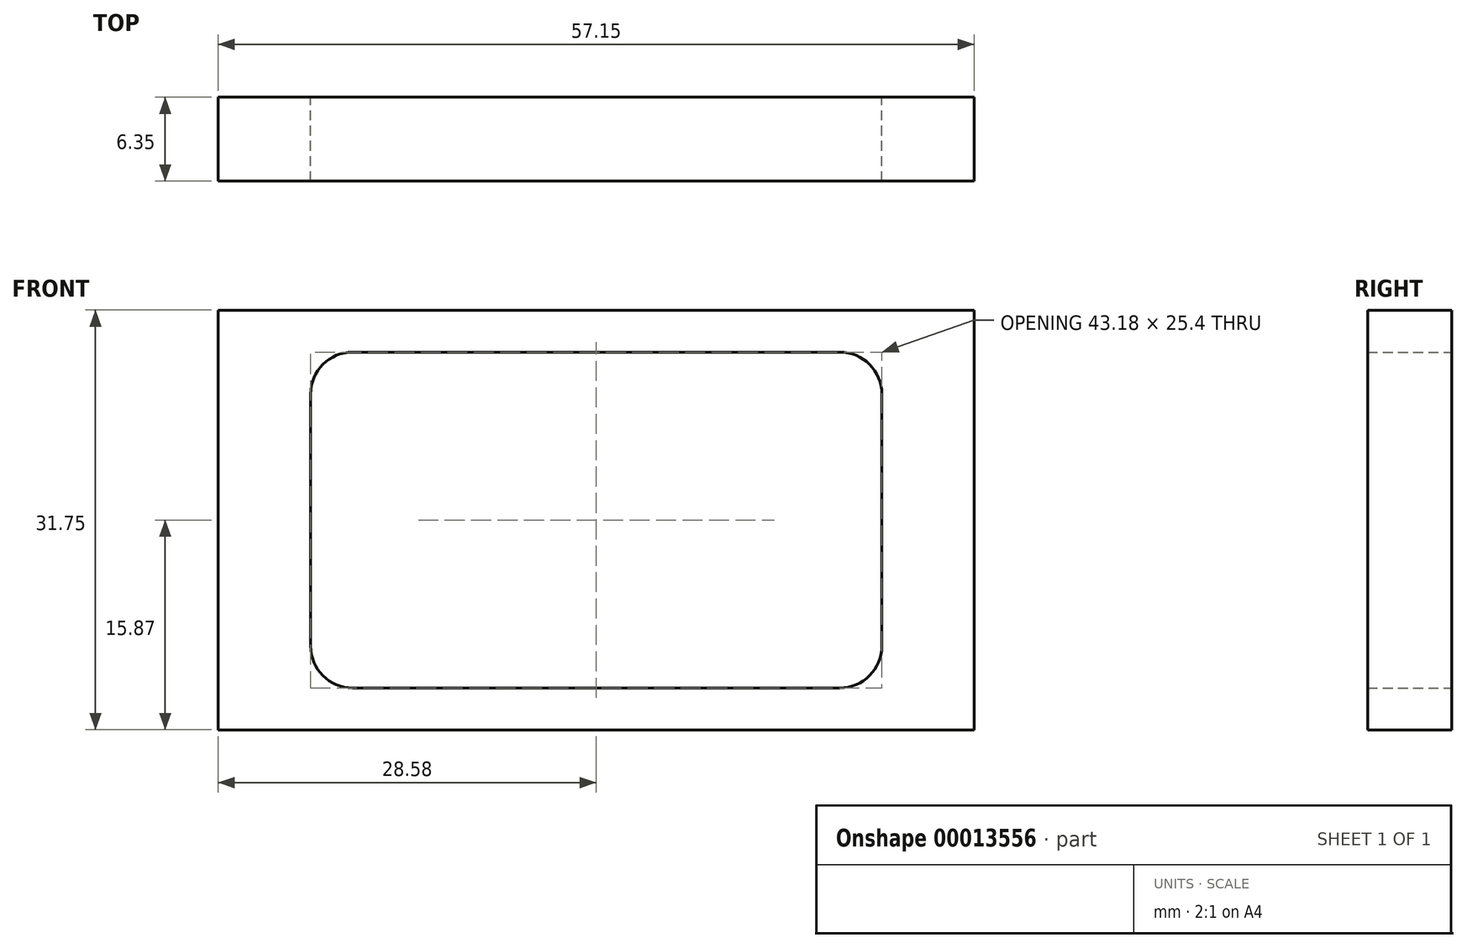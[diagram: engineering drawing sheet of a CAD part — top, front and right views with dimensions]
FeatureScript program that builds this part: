
annotation { "Feature Type Name" : "Feature", "Feature Type Description" : "" }
export const myFeature = defineFeature(function(context is Context, id is Id, definition is map)
    precondition{}
    {
        {
            var Q0;
            Q0=qCreatedBy(makeId("Front.planeOp"),FACE);
            var sketch = newSketch(context, id + "F0", { "sketchPlane" : qUnion([Q0])});
            skLineSegment(sketch, "E0.bottom", {"start": v(0, 0) * mm, "end": v(43.18, 0) * mm});
            skLineSegment(sketch, "E0.top", {"start": v(0, -25.4) * mm, "end": v(43.18, -25.4) * mm});
            skLineSegment(sketch, "E0.left", {"start": v(0, 0) * mm, "end": v(0, -25.4) * mm});
            skLineSegment(sketch, "E0.right", {"start": v(43.18, 0) * mm, "end": v(43.18, -25.4) * mm});
            skLineSegment(sketch, "E1.bottom", {"start": v(-6.99, 3.18) * mm, "end": v(50.17, 3.18) * mm});
            skLineSegment(sketch, "E1.top", {"start": v(-6.99, -28.58) * mm, "end": v(50.17, -28.58) * mm});
            skLineSegment(sketch, "E1.left", {"start": v(-6.99, 3.18) * mm, "end": v(-6.99, -28.58) * mm});
            skLineSegment(sketch, "E1.right", {"start": v(50.17, 3.18) * mm, "end": v(50.17, -28.58) * mm});
            skSolve(sketch);
        }
        {
            var Q0;
            Q0=makeQuery(id+"F0.imprint","IMPRINT",FACE,{"disambiguationData":[TD([[makeQuery(id+"F0.imprint","IMPRINT",EDGE,{"derivedFrom":sQuery(id+"F0.wireOp",EDGE,"E0.bottom")}),1.0]])]});
            extrude(context, id + "F1", {"entities" : qUnion([Q0]), "depth" : 6.35 * mm});
        }
        {
            var Q0;
            Q0=makeQuery(id+"F1.opExtrude","SWEPT_EDGE",EDGE,{"disambiguationData":[OSD([sQuery(id+"F0.wireOp",EDGE,"E0.bottom"),sQuery(id+"F0.wireOp",EDGE,"E0.left")])]});
            var Q1;
            Q1=makeQuery(id+"F1.opExtrude","SWEPT_EDGE",EDGE,{"disambiguationData":[OSD([sQuery(id+"F0.wireOp",EDGE,"E0.top"),sQuery(id+"F0.wireOp",EDGE,"E0.left")])]});
            var Q2;
            Q2=makeQuery(id+"F1.opExtrude","SWEPT_EDGE",EDGE,{"disambiguationData":[OSD([sQuery(id+"F0.wireOp",EDGE,"E0.top"),sQuery(id+"F0.wireOp",EDGE,"E0.right")])]});
            var Q3;
            Q3=makeQuery(id+"F1.opExtrude","SWEPT_EDGE",EDGE,{"disambiguationData":[OSD([sQuery(id+"F0.wireOp",EDGE,"E0.bottom"),sQuery(id+"F0.wireOp",EDGE,"E0.right")])]});
            fillet(context, id + "F2", {"entities" : qUnion([Q0, Q1, Q2, Q3]), "radius" : 3.17 * mm, "tangentPropagation" : true, "allowEdgeOverflow" : false});
        }
    });
